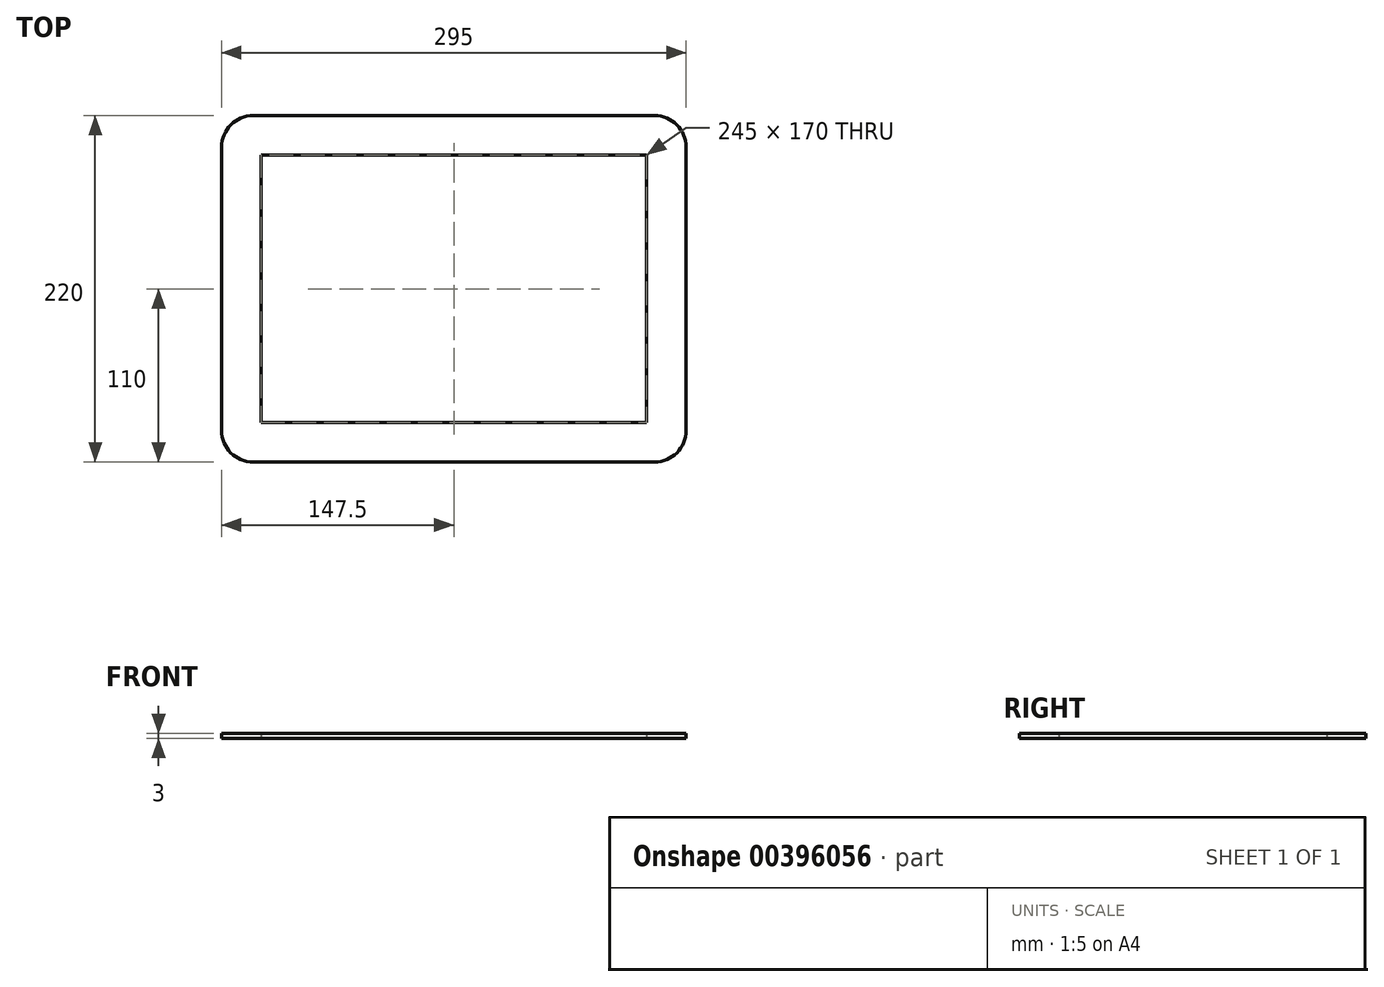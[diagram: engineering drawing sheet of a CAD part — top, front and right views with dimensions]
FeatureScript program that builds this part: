
annotation { "Feature Type Name" : "Feature", "Feature Type Description" : "" }
export const myFeature = defineFeature(function(context is Context, id is Id, definition is map)
    precondition{}
    {
        {
            var Q0;
            Q0=qCreatedBy(makeId("Top.planeOp"),FACE);
            var sketch = newSketch(context, id + "F0", { "sketchPlane" : qUnion([Q0])});
            skLineSegment(sketch, "E0.bottom", {"start": v(-127.5, 110) * mm, "end": v(127.5, 110) * mm});
            skLineSegment(sketch, "E0.top", {"start": v(-127.5, -110) * mm, "end": v(127.5, -110) * mm});
            skLineSegment(sketch, "E0.left", {"start": v(-147.5, 90) * mm, "end": v(-147.5, -90) * mm});
            skLineSegment(sketch, "E0.right", {"start": v(147.5, 90) * mm, "end": v(147.5, -90) * mm});
            skPoint(sketch, "E0.middle", {"position": v(0, 0) * mm});
            skPoint(sketch, "E1.visualSharp", {"position": v(-147.5, 110) * mm});
            skArc(sketch, "E1.filletArc", {"start": v(-127.5, 110) * mm, "mid": v(-141.64, 104.14) * mm, "end": v(-147.5, 90) * mm});
            skPoint(sketch, "E2.visualSharp", {"position": v(-147.5, -110) * mm});
            skArc(sketch, "E2.filletArc", {"start": v(-147.5, -90) * mm, "mid": v(-141.64, -104.14) * mm, "end": v(-127.5, -110) * mm});
            skPoint(sketch, "E3.visualSharp", {"position": v(147.5, -110) * mm});
            skArc(sketch, "E3.filletArc", {"start": v(127.5, -110) * mm, "mid": v(141.64, -104.14) * mm, "end": v(147.5, -90) * mm});
            skPoint(sketch, "E4.visualSharp", {"position": v(147.5, 110) * mm});
            skArc(sketch, "E4.filletArc", {"start": v(147.5, 90) * mm, "mid": v(141.64, 104.14) * mm, "end": v(127.5, 110) * mm});
            skLineSegment(sketch, "E5.bottom", {"start": v(-122.5, 85) * mm, "end": v(122.5, 85) * mm});
            skLineSegment(sketch, "E5.top", {"start": v(-122.5, -85) * mm, "end": v(122.5, -85) * mm});
            skLineSegment(sketch, "E5.left", {"start": v(-122.5, 85) * mm, "end": v(-122.5, -85) * mm});
            skLineSegment(sketch, "E5.right", {"start": v(122.5, 85) * mm, "end": v(122.5, -85) * mm});
            skSolve(sketch);
        }
        {
            var Q0;
            Q0 = qSketchRegion(id + "F0", true);
            extrude(context, id + "F1", {"entities" : qUnion([Q0]), "depth" : 3 * mm});
        }
    });
